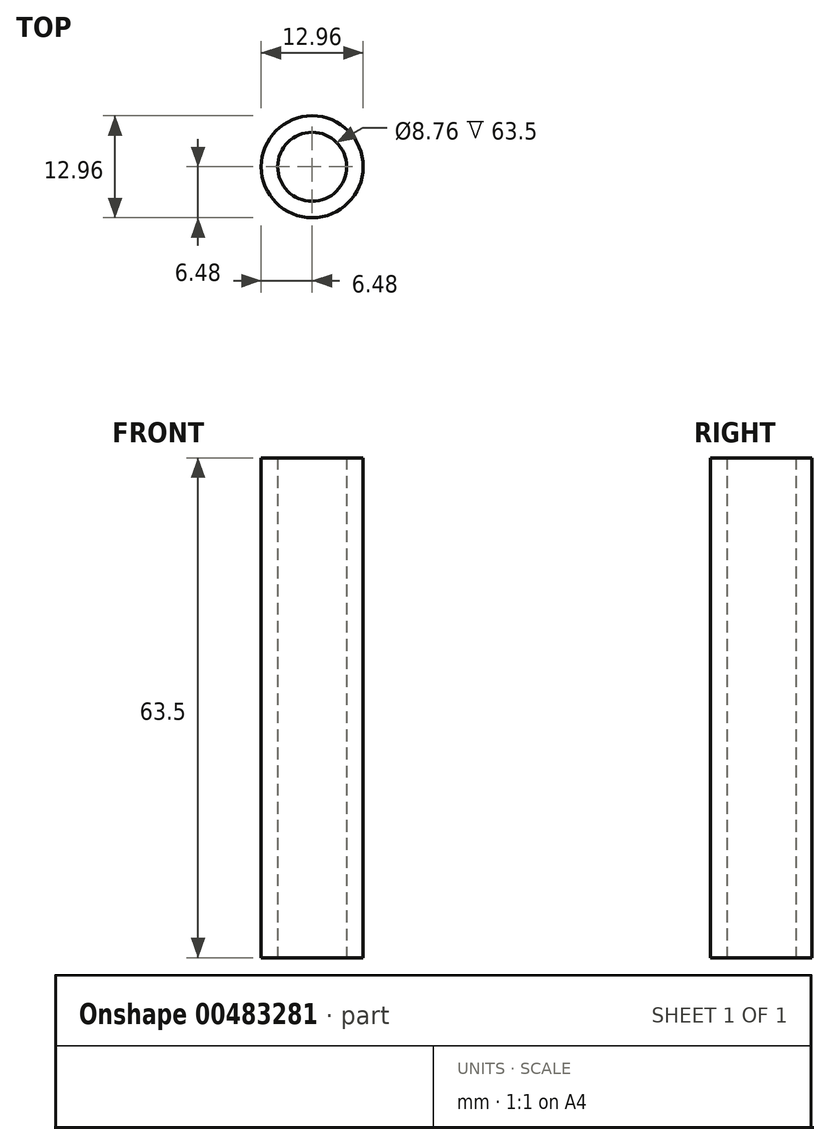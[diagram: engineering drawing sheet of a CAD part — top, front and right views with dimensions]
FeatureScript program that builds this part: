
annotation { "Feature Type Name" : "Feature", "Feature Type Description" : "" }
export const myFeature = defineFeature(function(context is Context, id is Id, definition is map)
    precondition{}
    {
        {
            var Q0;
            Q0=qCreatedBy(makeId("Top.planeOp"),FACE);
            var sketch = newSketch(context, id + "F0", { "sketchPlane" : qUnion([Q0])});
            skCircle(sketch, "E0", {"center": v(0, 0) * mm, "radius": 6.48 * mm});
            skCircle(sketch, "E1", {"center": v(0, 0) * mm, "radius": 4.38 * mm});
            skSolve(sketch);
        }
        {
            var Q0;
            Q0=makeQuery(id+"F0.imprint","IMPRINT",FACE,{"disambiguationData":[TD([[makeQuery(id+"F0.imprint","IMPRINT",EDGE,{"derivedFrom":sQuery(id+"F0.wireOp",EDGE,"E0")}),1.0]])]});
            extrude(context, id + "F1", {"entities" : qUnion([Q0]), "depth" : 63.5 * mm});
        }
    });
